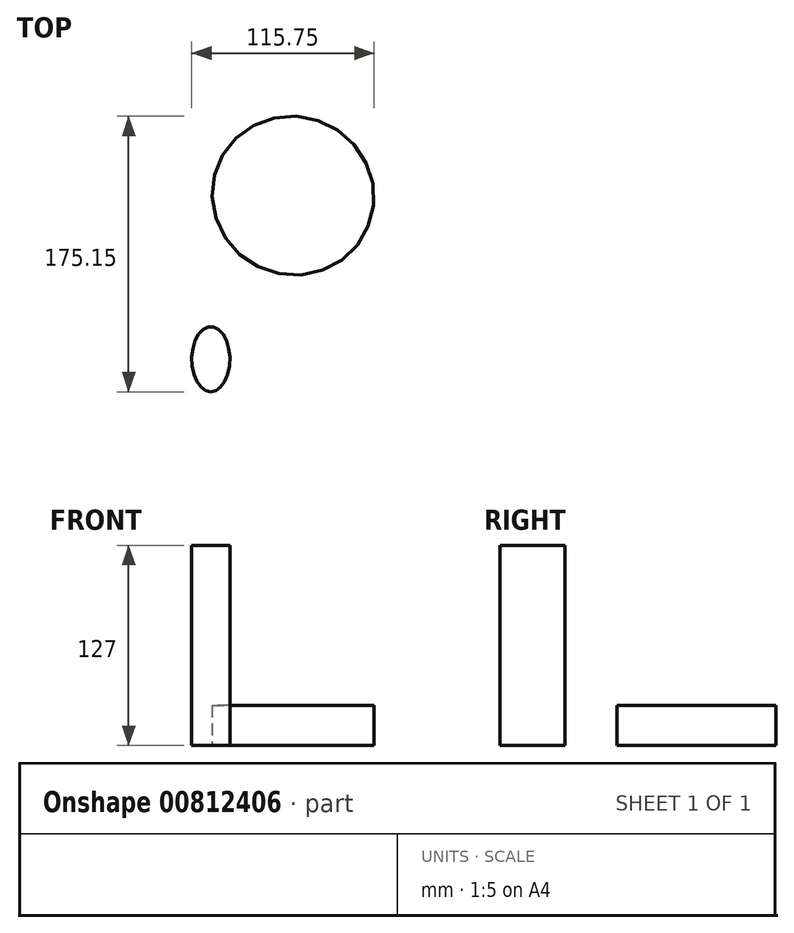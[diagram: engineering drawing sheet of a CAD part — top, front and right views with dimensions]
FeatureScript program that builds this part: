
annotation { "Feature Type Name" : "Feature", "Feature Type Description" : "" }
export const myFeature = defineFeature(function(context is Context, id is Id, definition is map)
    precondition{}
    {
        {
            var Q0;
            Q0=qCreatedBy(makeId("Top.planeOp"),FACE);
            var sketch = newSketch(context, id + "F0", { "sketchPlane" : qUnion([Q0])});
            skEllipse(sketch, "E0", {"center": v(4.18, 39.69) * mm, "majorRadius": 50.3 * mm, "minorRadius": 51.55 * mm, "majorAxis": v(-0.38, -0.93)});
            skSolve(sketch);
        }
        {
            var Q0;
            Q0=makeQuery(id+"F0.imprint","IMPRINT",FACE,{"disambiguationData":[TD([[makeQuery(id+"F0.imprint","IMPRINT",EDGE,{"derivedFrom":sQuery(id+"F0.wireOp",EDGE,"E0")}),1.0]])]});
            extrude(context, id + "F1", {"entities" : qUnion([Q0]), "depth" : 25.4 * mm, "offsetDistance" : 25.4 * mm});
        }
        {
            var Q0;
            Q0=qCreatedBy(makeId("Top.planeOp"),FACE);
            var sketch = newSketch(context, id + "F2", { "sketchPlane" : qUnion([Q0])});
            skEllipse(sketch, "E1", {"center": v(-48.08, -64.29) * mm, "majorRadius": 20.7 * mm, "minorRadius": 12.1 * mm, "majorAxis": v(0, -1)});
            skSolve(sketch);
        }
        {
            var Q0;
            Q0 = qSketchRegion(id + "F2", true);
            extrude(context, id + "F3", {"entities" : qUnion([Q0]), "depth" : 127 * mm, "offsetDistance" : 25.4 * mm});
        }
    });
